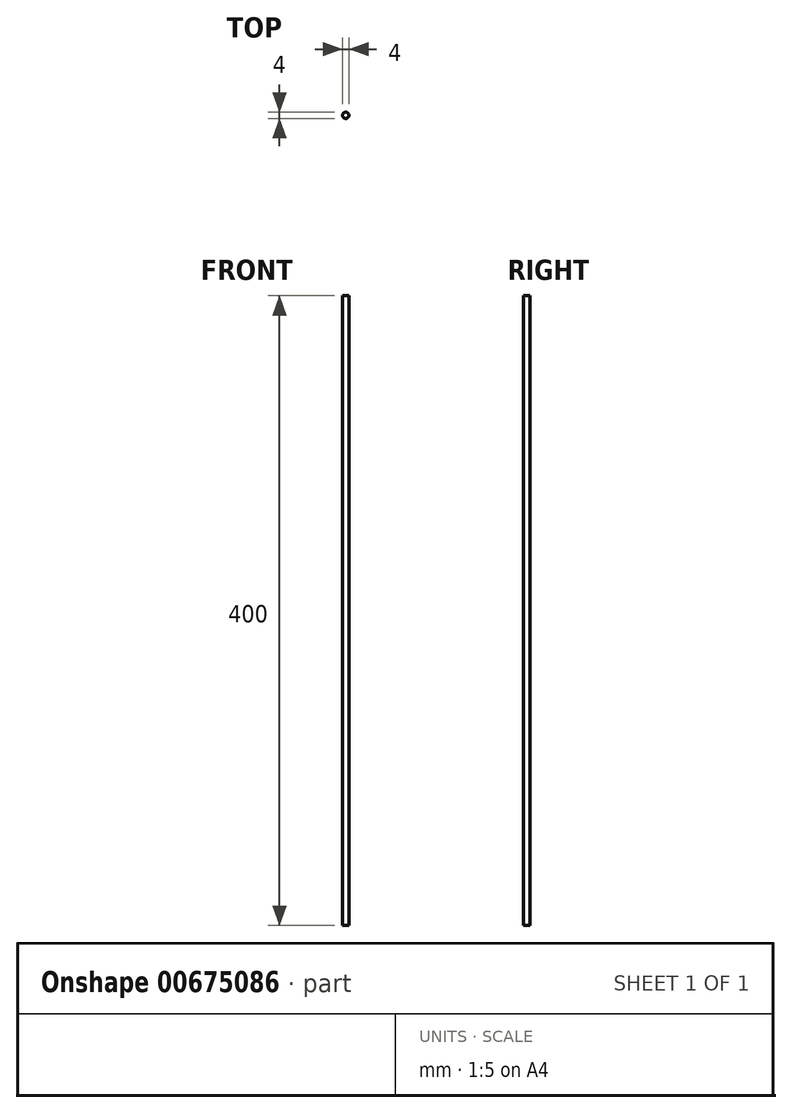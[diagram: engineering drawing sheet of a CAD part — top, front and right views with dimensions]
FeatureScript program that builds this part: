
annotation { "Feature Type Name" : "Feature", "Feature Type Description" : "" }
export const myFeature = defineFeature(function(context is Context, id is Id, definition is map)
    precondition{}
    {
        {
            var Q0;
            Q0=qCreatedBy(makeId("Top.planeOp"),FACE);
            var sketch = newSketch(context, id + "F0", { "sketchPlane" : qUnion([Q0])});
            skCircle(sketch, "E0", {"center": v(0, 0) * mm, "radius": 2 * mm});
            skSolve(sketch);
        }
        {
            var Q0;
            Q0=makeQuery(id+"F0.imprint","IMPRINT",FACE,{"disambiguationData":[TD([[makeQuery(id+"F0.imprint","IMPRINT",EDGE,{"derivedFrom":sQuery(id+"F0.wireOp",EDGE,"E0")}),1.0]])]});
            extrude(context, id + "F1", {"entities" : qUnion([Q0]), "endBound" : BoundingType.SYMMETRIC, "depth" : 400 * mm, "offsetDistance" : 25 * mm});
        }
    });
